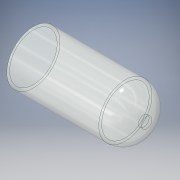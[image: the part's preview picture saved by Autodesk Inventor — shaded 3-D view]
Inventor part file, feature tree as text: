
AUTODESK INVENTOR PART (.ipt)
format: ipt  version: 2018 (Build 220112000, 112)  size: 139,264 bytes
history: native  units: in
note: dims shown in document units (in); Inventor stores cm internally (conversion verified against a paired STEP export)
features: extrude x1, fillet x1, shell x1, sketch x1
ambient origin geometry x8: Origin, YZ Plane, XZ Plane, XY Plane, X Axis, Y Axis, Z Axis, Center Point
bodies: Solid1 (feature_tree)
feature tree (4):
  extrude  "Extrusion1"  Depth=1.0in TaperAngle=0.0deg
  fillet  "Fillet1"  Radius=0.1875in
  shell  "Shell1"  Thickness=0.025in
  sketch  "Sketch1"  dims[d0=0.47in d1=1.0in d2=0.0in d3=0.1875in d4=0.025in]
